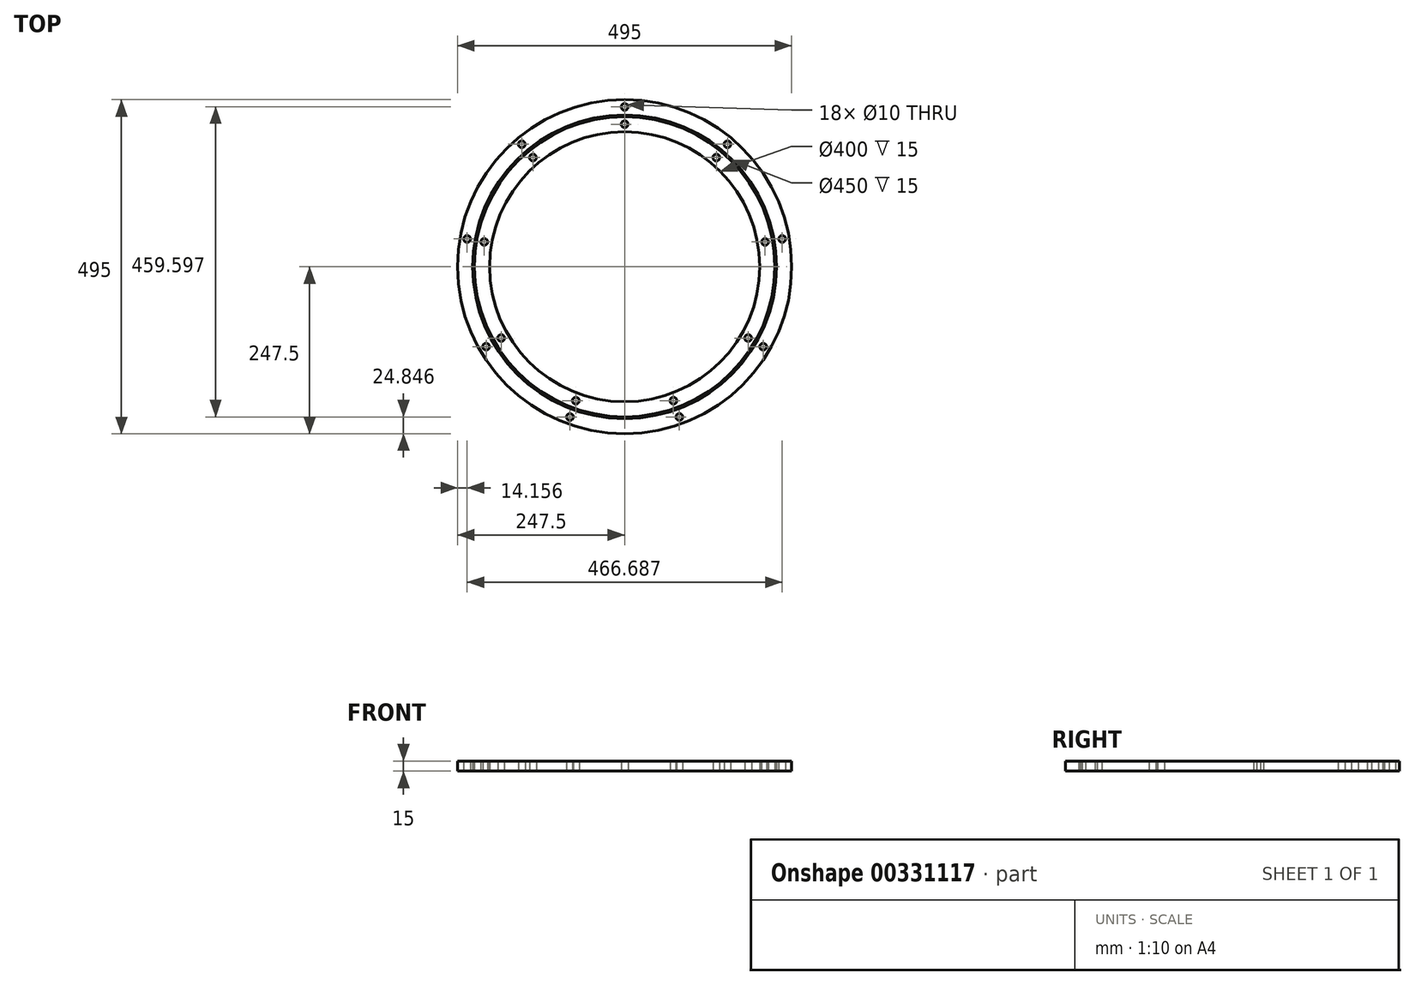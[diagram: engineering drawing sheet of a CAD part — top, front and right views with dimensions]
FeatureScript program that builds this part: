
annotation { "Feature Type Name" : "Feature", "Feature Type Description" : "" }
export const myFeature = defineFeature(function(context is Context, id is Id, definition is map)
    precondition{}
    {
        {
            var Q0;
            Q0=qCreatedBy(makeId("Top.planeOp"),FACE);
            var sketch = newSketch(context, id + "F0", { "sketchPlane" : qUnion([Q0])});
            skCircle(sketch, "E0", {"center": v(0, 0) * mm, "radius": 200 * mm});
            skCircle(sketch, "E1", {"center": v(0, 0) * mm, "radius": 222.5 * mm});
            skCircle(sketch, "E2", {"center": v(0, 0) * mm, "radius": 225 * mm});
            skCircle(sketch, "E3", {"center": v(0, 0) * mm, "radius": 247.5 * mm});
            skLineSegment(sketch, "E4", {"start": v(0, 0) * mm, "end": v(0, 265.43) * mm});
            skLineSegment(sketch, "E5", {"start": v(0, 200) * mm, "end": v(0, 211.25) * mm});
            skLineSegment(sketch, "E6", {"start": v(0, 225) * mm, "end": v(0, 236.94) * mm});
            skCircle(sketch, "E7", {"center": v(0, 236.94) * mm, "radius": 5 * mm});
            skCircle(sketch, "E8", {"center": v(0, 211.25) * mm, "radius": 5 * mm});
            skCircle(sketch, "E9.1.0", {"center": v(152.3, 181.5) * mm, "radius": 5 * mm});
            skCircle(sketch, "E9.1.1", {"center": v(135.79, 161.83) * mm, "radius": 5 * mm});
            skCircle(sketch, "E9.2.0", {"center": v(233.34, 41.14) * mm, "radius": 5 * mm});
            skCircle(sketch, "E9.2.1", {"center": v(208.04, 36.68) * mm, "radius": 5 * mm});
            skLineSegment(sketch, "E9.anchor1", {"start": v(0, 0) * mm, "end": v(0, 236.94) * mm, "construction": true});
            skLineSegment(sketch, "E9.anchor2", {"start": v(0, 0) * mm, "end": v(233.34, 41.14) * mm, "construction": true});
            skCircle(sketch, "E10.1.0", {"center": v(182.95, -105.62) * mm, "radius": 5 * mm});
            skCircle(sketch, "E10.1.1", {"center": v(205.2, -118.47) * mm, "radius": 5 * mm});
            skCircle(sketch, "E10.2.0", {"center": v(72.25, -198.51) * mm, "radius": 5 * mm});
            skCircle(sketch, "E10.2.1", {"center": v(81.04, -222.65) * mm, "radius": 5 * mm});
            skLineSegment(sketch, "E10.anchor1", {"start": v(0, 0) * mm, "end": v(208.04, 36.68) * mm, "construction": true});
            skLineSegment(sketch, "E10.anchor2", {"start": v(0, 0) * mm, "end": v(72.25, -198.51) * mm, "construction": true});
            skCircle(sketch, "E11.1.0", {"center": v(-81.04, -222.65) * mm, "radius": 5 * mm});
            skCircle(sketch, "E11.1.1", {"center": v(-72.25, -198.51) * mm, "radius": 5 * mm});
            skCircle(sketch, "E11.2.0", {"center": v(-205.2, -118.47) * mm, "radius": 5 * mm});
            skCircle(sketch, "E11.2.1", {"center": v(-182.95, -105.63) * mm, "radius": 5 * mm});
            skLineSegment(sketch, "E11.anchor1", {"start": v(0, 0) * mm, "end": v(81.04, -222.65) * mm, "construction": true});
            skLineSegment(sketch, "E11.anchor2", {"start": v(0, 0) * mm, "end": v(-205.2, -118.47) * mm, "construction": true});
            skCircle(sketch, "E12.1.0", {"center": v(-208.04, 36.68) * mm, "radius": 5 * mm});
            skCircle(sketch, "E12.1.1", {"center": v(-233.34, 41.14) * mm, "radius": 5 * mm});
            skCircle(sketch, "E12.2.0", {"center": v(-135.79, 161.83) * mm, "radius": 5 * mm});
            skCircle(sketch, "E12.2.1", {"center": v(-152.3, 181.5) * mm, "radius": 5 * mm});
            skLineSegment(sketch, "E12.anchor1", {"start": v(0, 0) * mm, "end": v(-182.95, -105.63) * mm, "construction": true});
            skLineSegment(sketch, "E12.anchor2", {"start": v(0, 0) * mm, "end": v(-135.79, 161.83) * mm, "construction": true});
            skSolve(sketch);
        }
        {
            var Q0;
            Q0=makeQuery(id+"F0.imprint","IMPRINT",FACE,{"disambiguationData":[TD([[makeQuery(id+"F0.imprint","IMPRINT",EDGE,{"derivedFrom":sQuery(id+"F0.wireOp",EDGE,"E0")}),-1.0]])]});
            var Q1;
            Q1=makeQuery(id+"F0.imprint","IMPRINT",FACE,{"disambiguationData":[TD([[makeQuery(id+"F0.imprint","IMPRINT",EDGE,{"derivedFrom":sQuery(id+"F0.wireOp",EDGE,"E2")}),-1.0]])]});
            extrude(context, id + "F1", {"entities" : qUnion([Q0, Q1]), "depth" : 15 * mm});
        }
    });
